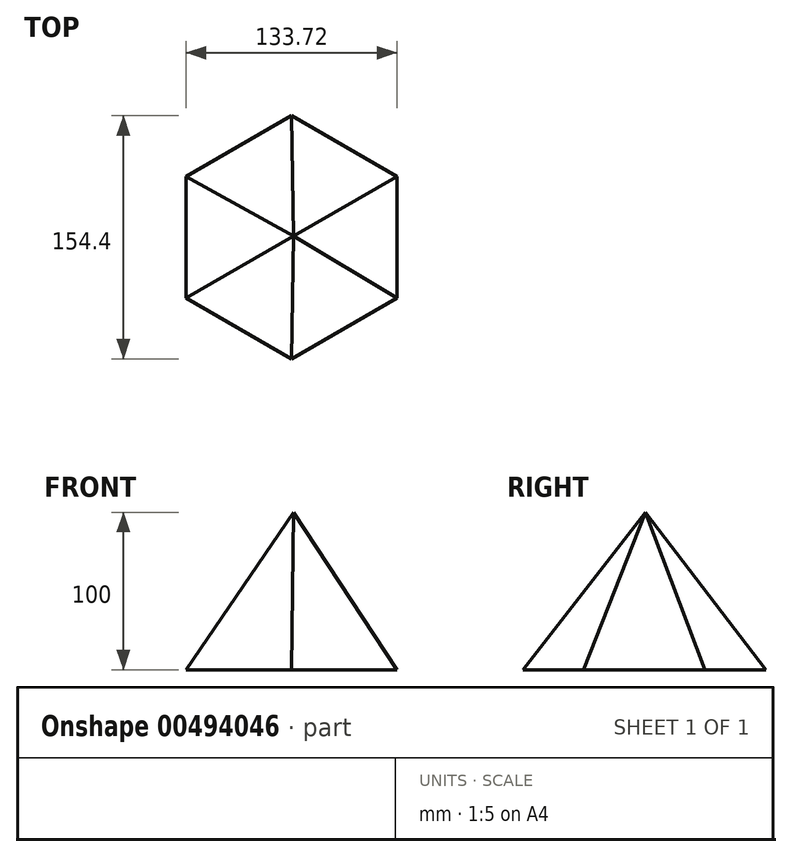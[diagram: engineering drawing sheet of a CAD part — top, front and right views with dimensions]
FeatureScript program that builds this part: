
annotation { "Feature Type Name" : "Feature", "Feature Type Description" : "" }
export const myFeature = defineFeature(function(context is Context, id is Id, definition is map)
    precondition{}
    {
        {
            var Q0;
            Q0=qCreatedBy(makeId("Top.planeOp"),FACE);
            var sketch = newSketch(context, id + "F0", { "sketchPlane" : qUnion([Q0])});
            skCircle(sketch, "E0.cCircle", {"center": v(0, 0) * mm, "radius": 77.2 * mm, "construction": true});
            skLineSegment(sketch, "E0.0", {"start": v(0, 77.2) * mm, "end": v(66.86, 38.6) * mm});
            skLineSegment(sketch, "E0.1", {"start": v(66.86, 38.6) * mm, "end": v(66.86, -38.6) * mm});
            skLineSegment(sketch, "E0.2", {"start": v(66.86, -38.6) * mm, "end": v(0, -77.2) * mm});
            skLineSegment(sketch, "E0.3", {"start": v(0, -77.2) * mm, "end": v(-66.86, -38.6) * mm});
            skLineSegment(sketch, "E0.4", {"start": v(-66.86, -38.6) * mm, "end": v(-66.86, 38.6) * mm});
            skLineSegment(sketch, "E0.5", {"start": v(-66.86, 38.6) * mm, "end": v(0, 77.2) * mm});
            skSolve(sketch);
        }
        {
            var Q0;
            Q0=qCreatedBy(makeId("Top.planeOp"),FACE);
            cPlane(context, id + "F1", {"entities" : qUnion([Q0]), "cplaneType" : CPlaneType.OFFSET, "offset" : 100 * mm, "width" : 150 * mm, "height" : 150 * mm});
        }
        {
            var Q0;
            Q0=qCreatedBy(id+"F1.planeOp",FACE);
            var sketch = newSketch(context, id + "F2", { "sketchPlane" : qUnion([Q0])});
            skPoint(sketch, "E1", {"position": v(1.15, 0.72) * mm});
            skSolve(sketch);
        }
        {
            var Q0;
            Q0=makeQuery(id+"F0.imprint","IMPRINT",FACE,{"disambiguationData":[TD([[makeQuery(id+"F0.imprint","IMPRINT",EDGE,{"derivedFrom":sQuery(id+"F0.wireOp",EDGE,"E0.0")}),-1.0]])]});
            var Q1;
            Q1=sQuery(id+"F2.wireOp",VERTEX,"E1");
            loft(context, id + "F3", {"sheetProfilesArray" : [{ "sheetProfileEntities" : qUnion([Q0]) }, { "sheetProfileEntities" : qUnion([Q1]) }]});
        }
    });
